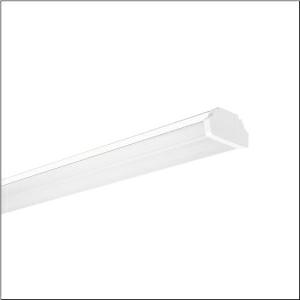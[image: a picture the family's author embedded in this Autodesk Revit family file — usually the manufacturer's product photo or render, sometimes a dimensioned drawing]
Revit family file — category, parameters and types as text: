
# Revit family: modario_31_gen_2_53bm812mv4a5c2_9e3d
name_source: partatom
category: Lighting Fixtures
units: mm (PartAtom-declared; Revit-internal decimal feet)

## family parameters
Cut with Voids When Loaded = No
Host = Face
Light Source = No
Part Type = Normal
Room Calculation Point = No
Round Connector Dimension = Use Diameter
Shared = No

## types (1)
- --- (1 x LED, 10960 lm, 60.5 W, 4000K)
    Apparent Load = 61 VA
    CIE Flux Codes = 47 80 95 93 100
    Color Rendering = 80
    Color Temperature = 4000K
    Default Elevation = 1800 mm
    Description = Modario 31 Gen.2, luminaire insert, of sheet steel, coil coated, white, length: 1.495mm, width: 81mm, height: 82mm, 5x system unit, system units: 299mm, LED rated luminous flux: 10.960lm, light colour: 840, SDCM (Standard Deviation of Colour Matching)MacAdam ≤ 3 SDCM (initial), control gear: ON/OFF Multilumen, control gear: ECG, with plug, 3-pole, with phase selection, mains connection: 220..240V, AC, 50/60Hz, rated input power: 61W, through-wiring accessed according to module size, primary optical cover: cover, of PMMA, light emission: direct distribution, primary light characteristic: symmetric, protection rating (complete): IP20, protection rating (LED compartment): IP50, insulation class (complete): insulation class I (protective earthing), certification: CE, ENEC, VDE, UKCA, impact resistance: IK03, permissible ambient temperature for indoor applications: -35..+40°C, corresponds to IFS (International Featured Standards) requirements for safety and quality in the food industry, reducing of maximum allowable ambient temperature of 5°C with ceiling mounting, IP40 when using the optional accessory 5TP9018, packaging unit: 1 piece
    Height = 92 mm
    Lamp = 1 x LED
    Lamp Light Flux = 10960 lm
    Lamp Power = 60.5 W
    Lamp count = 1
    Length = 1495 mm
    Luminous efficacy = 181 lm/W
    Manufacturer = Siteco
    ModVariant = No
    Model = 53BM812MV4A5C2
    Mounting Place = Ceiling
    Mounting Type = Pendant
    Number of Poles = 1
    OnlyDefault = Yes
    Power Factor = 1
    Product Name = Modario 31 Gen.2
    Product group = luminaire insert | ceiling pendant
    ProductGroupID = 901
    Protection Class = Protection class I
    Protection Degree = IP 20
    RLX_Detail_Level = 1
    RLX_Emergency_Light_Flux = 0 lm
    RLX_Emergency_Type = 0
    RLX_Emergency_Type_DB = No
    RlxData = <blob elided: 39853 chars, md5=2aba8b8a>
    Socket = socket
    Standby Power = 0 W
    System Light Flux = 10960 lm
    System Power = 61 W
    Type Comments = factory setting: luminous flux: 100 % | (A | C | E) | 140 mA
    Type Image = l_1341886.jpg
    URL = http://relux.com
    VarID = @adj_052395
    Voltage = 0 V
    Weight = 0.00 kg
    Width = 81 mm

## geometry (parser evidence)
native form markers: Blend x4, Sweep x10
no freeform markers — native parametric forms only
